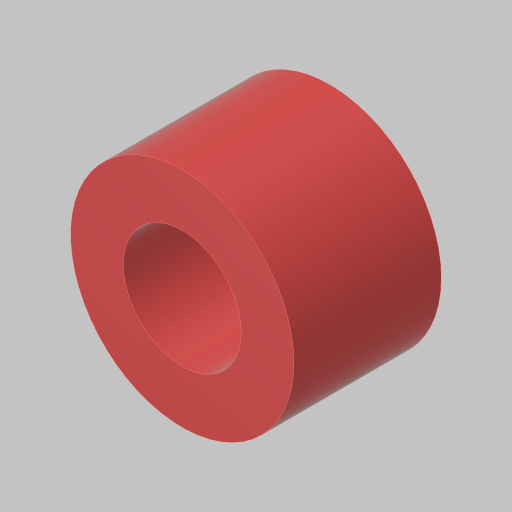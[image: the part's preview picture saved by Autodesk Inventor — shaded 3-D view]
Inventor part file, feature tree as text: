
AUTODESK INVENTOR PART (.ipt)
format: ipt  version: 2023.5 (Build 275446000, 446)  size: 117,248 bytes
history: native  units: in
note: dims shown in document units (in); Inventor stores cm internally (conversion verified against a paired STEP export)
features: extrude x1, sketch x1
ambient origin geometry x8: Origin, YZ Plane, XZ Plane, XY Plane, X Axis, Y Axis, Z Axis, Center Point
bodies: Solid1 (feature_tree)
feature tree (2):
  extrude  "Extrusion1"  Depth=0.7in
  sketch  "Sketch1"  dims[d0=0.56in d1=0.25in d2=0.7in d3=0.0in]
